# Revit family: CSR
name_source: partatom
category: Lighting Fixtures
units: mm (PartAtom-declared; Revit-internal decimal feet)

## family parameters
Cut with Voids When Loaded = No
Host = Face
Light Source = No
OmniClass Number = 23.80.70.11.21
OmniClass Title = Emergency Lighting
Part Type = Normal
Room Calculation Point = No
Round Connector Dimension = Use Diameter
Shared = No

## types (1)
- CSRIV
    Apparent Load = 4 VA
    Application = The CSR Series can be applied in stair-wells, hallways,
offices and other commercial applications. Offers 120 or
220-240VAC input at 50/60HZ.
    Certification = UL924 Listed for Wet Location
NFPA 101 and NFPA 70
OSHA
CEC T20 Compliant
    Default Elevation = 48.000"
    Description = The Compass International Exit offers quality and value
with a compact and attractive LED based emergency
exit. The white housing is made of high impact UL flame
rated thermoplastic. Snap together canopy, housing
and removable chevrons for quick and easy installation.
Universal single or double-face with SALIDA panel.
    Double Face = No
    Features = • LED life-cycle of more than 10 years
• Molded-in template for Quick installation
• Meets International input voltage requirements
• Optional long-life 4.8V Nickel Cadmium battery for
90 minute emergency lighting
• Provided with test switch and AC-On indicator
• Canopy Included
    Finish = White
    Glass = light Glass
    Holder Material = Steel
    Lamp = LED Lamp
    Lens = Red Glass
    Load Classification = Lighting
    Manufacturer = Compass Products
    Model = CSRIV
    Single Face = Yes
    Type Comments = Exit Light
    URL = https://www.currentlighting.com
    Wall Plate Material = Black
    Warranty = 2 year full unit warranty
    Wattage Comments = 3.8W
    Watts = 4 W

## geometry (parser evidence)
native form markers: Blend x8, Sweep x2
no freeform markers — native parametric forms only
